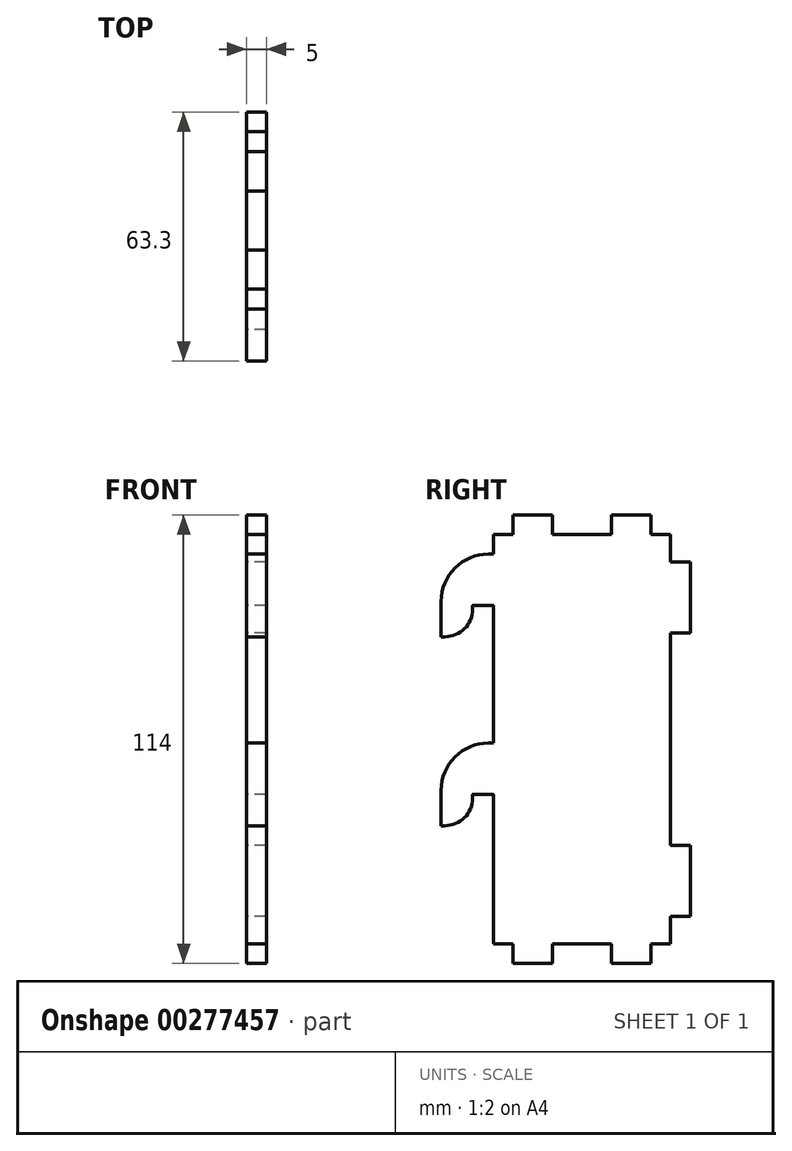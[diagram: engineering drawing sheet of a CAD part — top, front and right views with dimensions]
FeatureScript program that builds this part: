
annotation { "Feature Type Name" : "Feature", "Feature Type Description" : "" }
export const myFeature = defineFeature(function(context is Context, id is Id, definition is map)
    precondition{}
    {
        {
            var Q0;
            Q0=qCreatedBy(makeId("Right.planeOp"),FACE);
            var sketch = newSketch(context, id + "F0", { "sketchPlane" : qUnion([Q0])});
            skLineSegment(sketch, "E0.bottom", {"start": v(-22.5, 52) * mm, "end": v(-17.5, 52) * mm});
            skLineSegment(sketch, "E0.top", {"start": v(-22.5, -52) * mm, "end": v(-17.5, -52) * mm});
            skLineSegment(sketch, "E0.left", {"start": v(-22.5, 33.8) * mm, "end": v(-22.5, -1) * mm});
            skLineSegment(sketch, "E0.right", {"start": v(22.5, 52) * mm, "end": v(22.5, 45) * mm});
            skLineSegment(sketch, "E1.top", {"start": v(7.5, 57) * mm, "end": v(17.5, 57) * mm});
            skLineSegment(sketch, "E1.left", {"start": v(7.5, 52) * mm, "end": v(7.5, 57) * mm});
            skLineSegment(sketch, "E1.right", {"start": v(17.5, 52) * mm, "end": v(17.5, 57) * mm});
            skLineSegment(sketch, "E2.top", {"start": v(-17.5, 57) * mm, "end": v(-7.5, 57) * mm});
            skLineSegment(sketch, "E2.left", {"start": v(-17.5, 52) * mm, "end": v(-17.5, 57) * mm});
            skLineSegment(sketch, "E2.right", {"start": v(-7.5, 52) * mm, "end": v(-7.5, 57) * mm});
            skLineSegment(sketch, "E3.top", {"start": v(-17.5, -57) * mm, "end": v(-7.5, -57) * mm});
            skLineSegment(sketch, "E3.left", {"start": v(-17.5, -52) * mm, "end": v(-17.5, -57) * mm});
            skLineSegment(sketch, "E3.right", {"start": v(-7.5, -52) * mm, "end": v(-7.5, -57) * mm});
            skLineSegment(sketch, "E4.top", {"start": v(7.5, -57) * mm, "end": v(17.5, -57) * mm});
            skLineSegment(sketch, "E4.left", {"start": v(7.5, -52) * mm, "end": v(7.5, -57) * mm});
            skLineSegment(sketch, "E4.right", {"start": v(17.5, -52) * mm, "end": v(17.5, -57) * mm});
            skLineSegment(sketch, "E5.bottom", {"start": v(22.5, 45) * mm, "end": v(27.5, 45) * mm});
            skLineSegment(sketch, "E5.top", {"start": v(22.5, 27) * mm, "end": v(27.5, 27) * mm});
            skLineSegment(sketch, "E5.right", {"start": v(27.5, 45) * mm, "end": v(27.5, 27) * mm});
            skLineSegment(sketch, "E6.bottom", {"start": v(22.5, -27) * mm, "end": v(27.5, -27) * mm});
            skLineSegment(sketch, "E6.top", {"start": v(22.5, -45) * mm, "end": v(27.5, -45) * mm});
            skLineSegment(sketch, "E6.right", {"start": v(27.5, -27) * mm, "end": v(27.5, -45) * mm});
            skLineSegment(sketch, "E7.trimOffspring", {"start": v(-7.5, 52) * mm, "end": v(7.5, 52) * mm});
            skLineSegment(sketch, "E8.trimOffspring", {"start": v(17.5, 52) * mm, "end": v(22.5, 52) * mm});
            skLineSegment(sketch, "E9.trimOffspring", {"start": v(17.5, -52) * mm, "end": v(22.5, -52) * mm});
            skLineSegment(sketch, "E10.trimOffspring", {"start": v(-7.5, -52) * mm, "end": v(7.5, -52) * mm});
            skLineSegment(sketch, "E11.trimOffspring", {"start": v(22.5, 27) * mm, "end": v(22.5, -27) * mm});
            skLineSegment(sketch, "E12.trimOffspring", {"start": v(22.5, -45) * mm, "end": v(22.5, -52) * mm});
            skLineSegment(sketch, "E13", {"start": v(-23.8, 47) * mm, "end": v(-23.8, 47) * mm});
            skLineSegment(sketch, "E14", {"start": v(-35.8, 35) * mm, "end": v(-35.8, 26) * mm});
            skLineSegment(sketch, "E15", {"start": v(-35.8, 26) * mm, "end": v(-34.8, 26) * mm});
            skLineSegment(sketch, "E16", {"start": v(-27.8, 33) * mm, "end": v(-27.8, 33.8) * mm});
            skLineSegment(sketch, "E17", {"start": v(-27.6, 34) * mm, "end": v(-22.7, 34) * mm});
            skPoint(sketch, "E18.visualSharp", {"position": v(-35.8, 47) * mm});
            skArc(sketch, "E18.filletArc", {"start": v(-23.8, 47) * mm, "mid": v(-32.29, 43.49) * mm, "end": v(-35.8, 35) * mm});
            skPoint(sketch, "E19.visualSharp", {"position": v(-27.8, 26) * mm});
            skArc(sketch, "E19.filletArc", {"start": v(-34.8, 26) * mm, "mid": v(-29.85, 28.05) * mm, "end": v(-27.8, 33) * mm});
            skLineSegment(sketch, "E20", {"start": v(-22.5, -1) * mm, "end": v(-23.8, -1) * mm});
            skLineSegment(sketch, "E21", {"start": v(-23.8, -1) * mm, "end": v(-23.8, -1) * mm});
            skLineSegment(sketch, "E22", {"start": v(-35.8, -13) * mm, "end": v(-35.8, -22) * mm});
            skLineSegment(sketch, "E23", {"start": v(-35.8, -22) * mm, "end": v(-34.8, -22) * mm});
            skLineSegment(sketch, "E24", {"start": v(-34.8, -22) * mm, "end": v(-34.8, -22) * mm});
            skLineSegment(sketch, "E25", {"start": v(-27.8, -15) * mm, "end": v(-27.8, -14.2) * mm});
            skLineSegment(sketch, "E26", {"start": v(-27.6, -14) * mm, "end": v(-22.7, -14) * mm});
            skPoint(sketch, "E27.visualSharp", {"position": v(-35.8, -1) * mm});
            skArc(sketch, "E27.filletArc", {"start": v(-23.8, -1) * mm, "mid": v(-32.29, -4.51) * mm, "end": v(-35.8, -13) * mm});
            skPoint(sketch, "E28.visualSharp", {"position": v(-27.8, -22) * mm});
            skArc(sketch, "E28.filletArc", {"start": v(-34.8, -22) * mm, "mid": v(-29.85, -19.95) * mm, "end": v(-27.8, -15) * mm});
            skPoint(sketch, "E29.visualSharp", {"position": v(-27.8, 34) * mm});
            skArc(sketch, "E29.filletArc", {"start": v(-27.6, 34) * mm, "mid": v(-27.74, 33.94) * mm, "end": v(-27.8, 33.8) * mm});
            skPoint(sketch, "E30.visualSharp", {"position": v(-22.5, 34) * mm});
            skArc(sketch, "E30.filletArc", {"start": v(-22.5, 33.8) * mm, "mid": v(-22.56, 33.94) * mm, "end": v(-22.7, 34) * mm});
            skLineSegment(sketch, "E31.trimOffspring", {"start": v(-22.5, -14.2) * mm, "end": v(-22.5, -52) * mm});
            skPoint(sketch, "E32.visualSharp", {"position": v(-27.8, -14) * mm});
            skArc(sketch, "E32.filletArc", {"start": v(-27.6, -14) * mm, "mid": v(-27.74, -14.06) * mm, "end": v(-27.8, -14.2) * mm});
            skPoint(sketch, "E33.visualSharp", {"position": v(-22.5, -14) * mm});
            skArc(sketch, "E33.filletArc", {"start": v(-22.5, -14.2) * mm, "mid": v(-22.56, -14.06) * mm, "end": v(-22.7, -14) * mm});
            skLineSegment(sketch, "E34", {"start": v(-22.5, 52) * mm, "end": v(-22.5, 47) * mm});
            skLineSegment(sketch, "E35", {"start": v(-22.5, 47) * mm, "end": v(-23.8, 47) * mm});
            skSolve(sketch);
        }
        {
            var Q0;
            Q0=makeQuery(id+"F0.imprint","IMPRINT",FACE,{"disambiguationData":[TD([[makeQuery(id+"F0.imprint","IMPRINT",EDGE,{"derivedFrom":sQuery(id+"F0.wireOp",EDGE,"E0.bottom")}),-1.0]])]});
            extrude(context, id + "F1", {"entities" : qUnion([Q0]), "depth" : 5 * mm});
        }
    });
